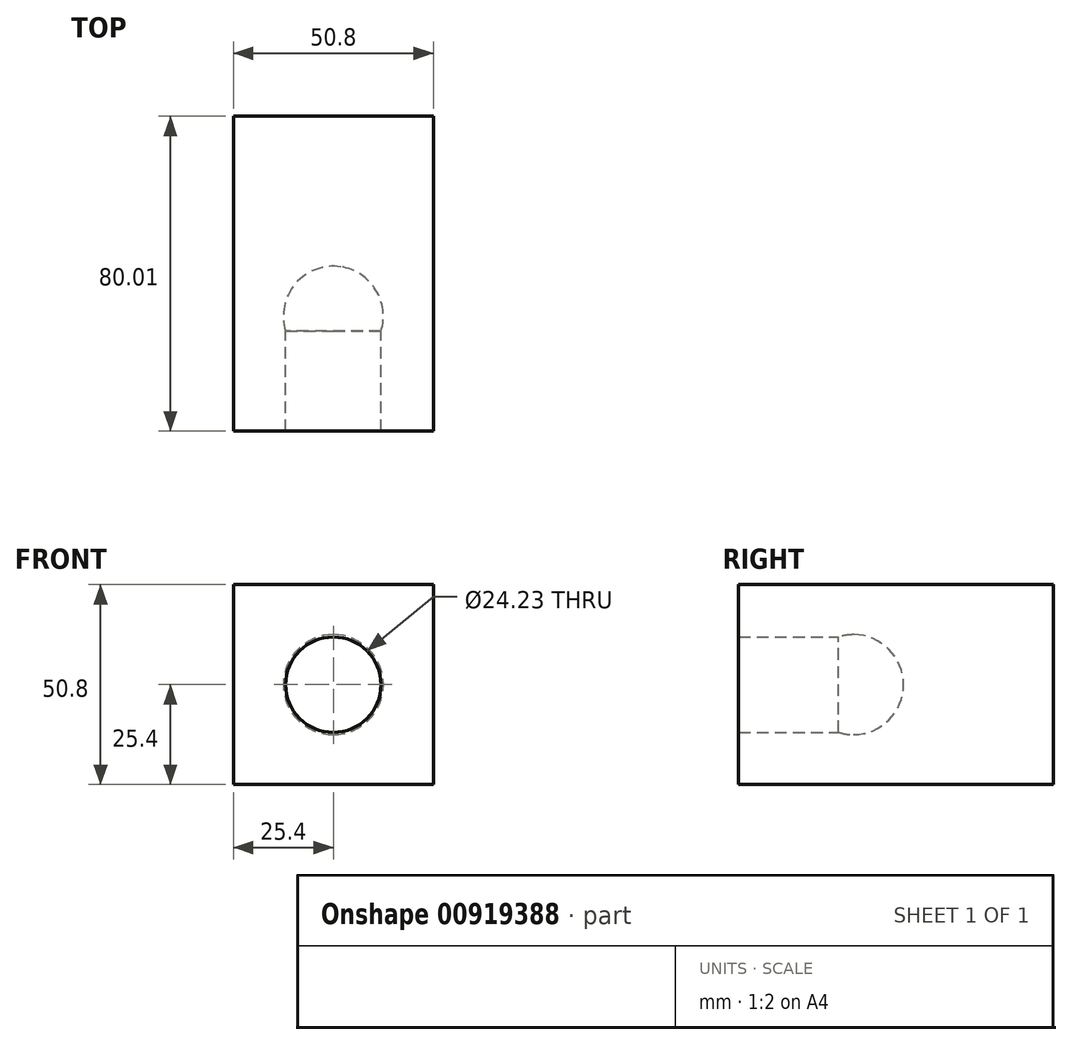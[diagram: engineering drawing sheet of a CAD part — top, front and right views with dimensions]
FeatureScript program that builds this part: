
annotation { "Feature Type Name" : "Feature", "Feature Type Description" : "" }
export const myFeature = defineFeature(function(context is Context, id is Id, definition is map)
    precondition{}
    {
        {
            var Q0;
            Q0=qCreatedBy(makeId("Front.planeOp"),FACE);
            var sketch = newSketch(context, id + "F0", { "sketchPlane" : qUnion([Q0])});
            skLineSegment(sketch, "E0", {"start": v(0, 80.03) * mm, "end": v(0, -94.1) * mm});
            skLineSegment(sketch, "E1.bottom", {"start": v(-25.4, 25.4) * mm, "end": v(25.4, 25.4) * mm});
            skLineSegment(sketch, "E1.top", {"start": v(-25.4, -25.4) * mm, "end": v(25.4, -25.4) * mm});
            skLineSegment(sketch, "E1.left", {"start": v(-25.4, 25.4) * mm, "end": v(-25.4, -25.4) * mm});
            skLineSegment(sketch, "E1.right", {"start": v(25.4, 25.4) * mm, "end": v(25.4, -25.4) * mm});
            skPoint(sketch, "E1.middle", {"position": v(0, 0) * mm});
            skSolve(sketch);
        }
        {
            var Q0;
            {var subQ5=sQuery(id+"F0.wireOp",EDGE,"E1.left");Q0=makeQuery(id+"F0.imprint","IMPRINT",FACE,{"disambiguationData":[TD([[makeQuery(id+"F0.imprint","IMPRINT",EDGE,{"derivedFrom":subQ5}),1.0]])]});}
            var Q1;
            {var subQ5=sQuery(id+"F0.wireOp",EDGE,"E1.right");Q1=makeQuery(id+"F0.imprint","IMPRINT",FACE,{"disambiguationData":[TD([[makeQuery(id+"F0.imprint","IMPRINT",EDGE,{"derivedFrom":subQ5}),-1.0]])]});}
            extrude(context, id + "F1", {"entities" : qUnion([Q0, Q1]), "depth" : 50.8 * mm, "offsetDistance" : 25.4 * mm, "symmetric" : true});
        }
        {
            var Q0;
            Q0=makeQuery(id+"F1.opExtrude","CAP_FACE",FACE,{"disambiguationData":[OSD([sQuery(id+"F0.wireOp",EDGE,"E1.bottom"),sQuery(id+"F0.wireOp",EDGE,"E1.top"),sQuery(id+"F0.wireOp",EDGE,"E1.left"),sQuery(id+"F0.wireOp",EDGE,"E1.right")])],"isStart":false});
            var sketch = newSketch(context, id + "F2", { "sketchPlane" : qUnion([Q0])});
            skCircle(sketch, "E2", {"center": v(0, 0) * mm, "radius": 12.7 * mm});
            skLineSegment(sketch, "E3", {"start": v(0, 43.8) * mm, "end": v(0, -58.6) * mm});
            skSolve(sketch);
        }
        {
            var Q0;
            {var subQ8=makeQuery(id+"F1.opExtrude","CAP_EDGE",EDGE,{"disambiguationData":[OSD([sQuery(id+"F0.wireOp",EDGE,"E1.left")])],"isStart":false});Q0=makeQuery(id+"F2.imprint","IMPRINT",FACE,{"disambiguationData":[TD([[makeQuery(id+"F2.imprint","IMPRINT",EDGE,{"derivedFrom":subQ8}),1.0]])]});}
            var Q1;
            {var subQ8=makeQuery(id+"F1.opExtrude","CAP_EDGE",EDGE,{"disambiguationData":[OSD([sQuery(id+"F0.wireOp",EDGE,"E1.right")])],"isStart":false});Q1=makeQuery(id+"F2.imprint","IMPRINT",FACE,{"disambiguationData":[TD([[makeQuery(id+"F2.imprint","IMPRINT",EDGE,{"derivedFrom":subQ8}),-1.0]])]});}
            var Q2;
            {var subQ0=sQuery(id+"F2.wireOp",EDGE,"E3");var subQ1=sQuery(id+"F2.wireOp",EDGE,"E2");var subQ2=makeQuery(id+"F2.imprint","INTERSECT",VERTEX,{"disambiguationData":[OD(0.0)],"derivedFrom":[subQ1,subQ0]});Q2=makeQuery(id+"F2.imprint","IMPRINT",FACE,{"disambiguationData":[TD([[makeQuery(id+"F2.imprint","IMPRINT",EDGE,{"disambiguationData":[TD([[subQ2,-1.0]])],"derivedFrom":subQ1}),1.0]])]});}
            var Q3;
            {var subQ0=sQuery(id+"F2.wireOp",EDGE,"E3");var subQ1=sQuery(id+"F2.wireOp",EDGE,"E2");var subQ2=makeQuery(id+"F2.imprint","INTERSECT",VERTEX,{"disambiguationData":[OD(0.0)],"derivedFrom":[subQ1,subQ0]});Q3=makeQuery(id+"F2.imprint","IMPRINT",FACE,{"disambiguationData":[TD([[makeQuery(id+"F2.imprint","IMPRINT",EDGE,{"disambiguationData":[TD([[subQ2,1.0]])],"derivedFrom":subQ1}),1.0]])]});}
            extrude(context, id + "F3", {"entities" : qUnion([Q0, Q1, Q2, Q3]), "operationType" : NewBodyOperationType.ADD, "depth" : 25.4 * mm, "offsetDistance" : 25.4 * mm});
        }
        {
            var Q0;
            {var subQ0=sQuery(id+"F2.wireOp",EDGE,"E3");var subQ1=sQuery(id+"F2.wireOp",EDGE,"E2");var subQ2=makeQuery(id+"F2.imprint","INTERSECT",VERTEX,{"disambiguationData":[OD(0.0)],"derivedFrom":[subQ1,subQ0]});Q0=makeQuery(id+"F2.imprint","IMPRINT",FACE,{"disambiguationData":[TD([[makeQuery(id+"F2.imprint","IMPRINT",EDGE,{"disambiguationData":[TD([[subQ2,-1.0]])],"derivedFrom":subQ1}),1.0]])]});}
            var Q1;
            Q1=sQuery(id+"F2.wireOp",EDGE,"E3");
            revolve(context, id + "F4", {"operationType" : NewBodyOperationType.REMOVE, "surfaceOperationType" : NewSurfaceOperationType.NEW, "entities" : qUnion([Q0]), "axis" : qUnion([Q1]), "revolveType" : RevolveType.FULL});
        }
        {
            var Q0;
            Q0=makeQuery(id+"F3.opExtrude","CAP_FACE",FACE,{"disambiguationData":[OSD([sQuery(id+"F0.wireOp",EDGE,"E1.bottom"),sQuery(id+"F0.wireOp",EDGE,"E1.top"),sQuery(id+"F0.wireOp",EDGE,"E1.left"),sQuery(id+"F0.wireOp",EDGE,"E1.right")])],"isStart":false});
            extrude(context, id + "F5", {"entities" : qUnion([Q0]), "operationType" : NewBodyOperationType.REMOVE, "oppositeDirection" : true, "depth" : 21.59 * mm, "offsetDistance" : 25.4 * mm});
        }
        {
            var Q0;
            Q0=makeQuery(id+"F5.boolean.opBoolean","COPY",FACE,{"derivedFrom":makeQuery(id+"F5.opExtrude","CAP_FACE",FACE,{"disambiguationData":[OSD([sQuery(id+"F0.wireOp",EDGE,"E1.bottom"),sQuery(id+"F0.wireOp",EDGE,"E1.top"),sQuery(id+"F0.wireOp",EDGE,"E1.left"),sQuery(id+"F0.wireOp",EDGE,"E1.right")])],"isStart":false})});
            extrude(context, id + "F6", {"entities" : qUnion([Q0]), "operationType" : NewBodyOperationType.ADD, "depth" : 25.4 * mm, "offsetDistance" : 25.4 * mm});
        }
    });
